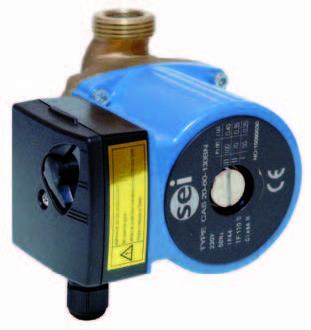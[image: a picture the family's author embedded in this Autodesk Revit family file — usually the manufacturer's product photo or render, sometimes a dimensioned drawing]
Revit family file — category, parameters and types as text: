
# Revit family: CAS_25-80BN-AC52154
name_source: partatom
category: Aparatos eléctricos
revit_build: Autodesk Revit 2016 (Build: 20150220_1215(x64)
units: mm (PartAtom-declared; Revit-internal decimal feet)

## family parameters
Compartido = No
Corte con vacíos al cargar = No
Cota de conector redondo = Diámetro de uso
Mantener orientación de anotación = No
Número OmniClass = 23.80.00.00
Punto de cálculo de habitación = No
Se basa en plano de trabajo = No
Siempre vertical = Sí
Tipo de pieza = Caja de conexiones
Título OmniClass = Electric Power and Lighting

## types (2) — shared parameters
Fabricante = SALVADOR ESCODA
URL = www.salvadorescoda.com
zero-valued in all types: Costo

## per-type parameters (varying)
| type | Aislamiento | Caudal | Conexión racores | Código de montaje | Descripción | Dimensiones Unidad Interior | Imagen de tipo | Intensidad máx. | Modelo | Motor | Máx. presión trabajo | Peso | Potencia máx. | Presión disponible | Protección | Rango temperatura agua | Regulable | Temperatura ambiente |
| MVD-22T2 | 35 dB(A) |  |  | CL23370 | CONDUCTO BAJA SILUETA | 700 x 210 x 500 mm | <Ninguno> |  | MVD-22T2/DHN1-DA5 | 521 m3/h | 2,2kW / 39W | 17,5 kg neto |  |  | 6,35 mm (1/4") | 2,6kW / 39W |  | DC / WZDK100-38GS |
| CAS | Clase H | 3 m3/h | 1 1/2" DN | AC52154 | BOMBA CIRCULADORA PARA ACS | 160 x 180 x 150 mm | SEI_CAS.jpg | 1,10 A | CAS 25-80 BN | 2 polos, 1x230V - 50Hz | 10 bar | 3,5 Kgs | 230 W | 6 m.c.a. | IP44 | 2º a 110 ºC | 3 velocidades | Hasta 40ºC |
